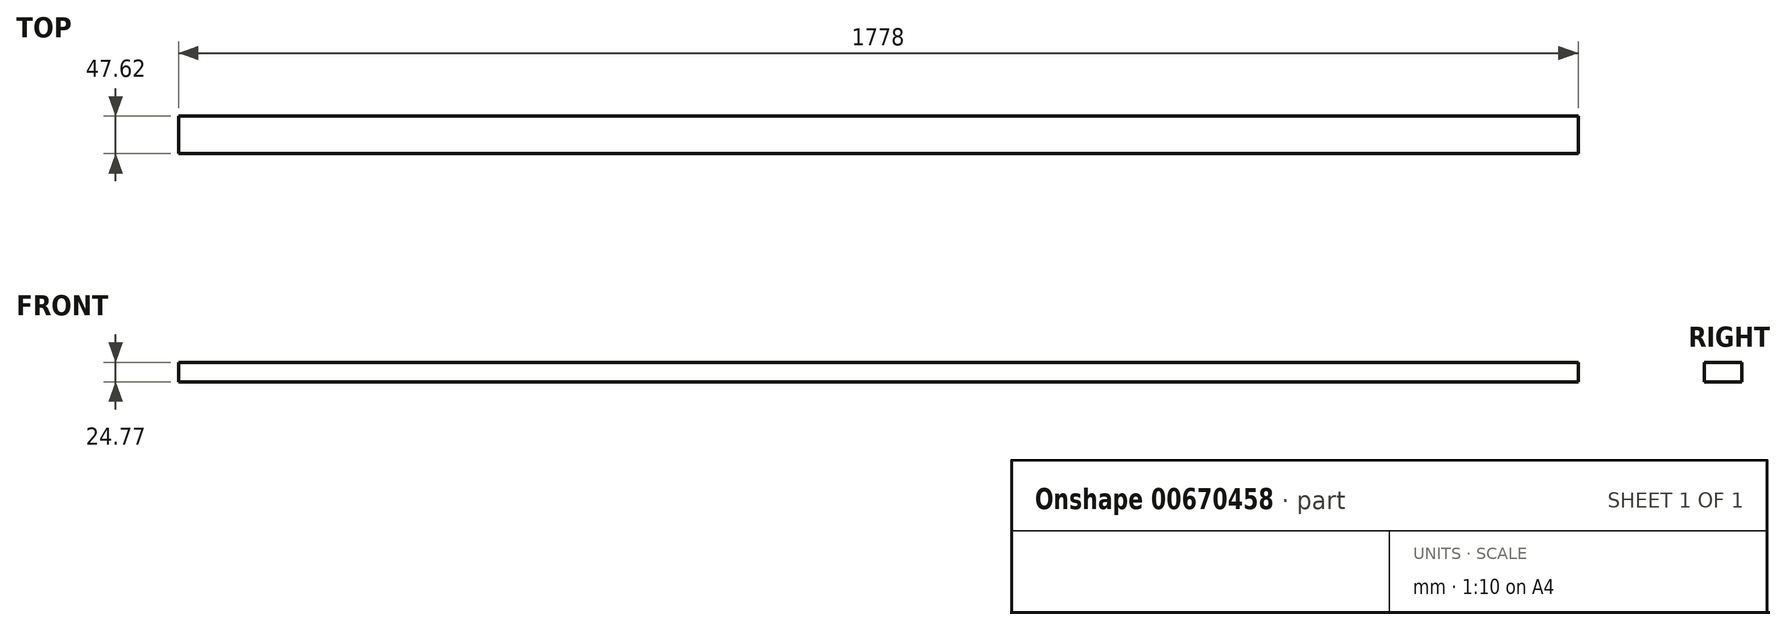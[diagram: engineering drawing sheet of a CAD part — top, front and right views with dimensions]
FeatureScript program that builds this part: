
annotation { "Feature Type Name" : "Feature", "Feature Type Description" : "" }
export const myFeature = defineFeature(function(context is Context, id is Id, definition is map)
    precondition{}
    {
        {
            var Q0;
            Q0=qCreatedBy(makeId("Top.planeOp"),FACE);
            var sketch = newSketch(context, id + "F0", { "sketchPlane" : qUnion([Q0])});
            skLineSegment(sketch, "E0.bottom", {"start": v(0, 0) * mm, "end": v(-1778, 0) * mm});
            skLineSegment(sketch, "E0.top", {"start": v(0, 47.63) * mm, "end": v(-1778, 47.62) * mm});
            skLineSegment(sketch, "E0.left", {"start": v(0, 0) * mm, "end": v(0, 47.63) * mm});
            skLineSegment(sketch, "E0.right", {"start": v(-1778, 0) * mm, "end": v(-1778, 47.62) * mm});
            skSolve(sketch);
        }
        {
            var Q0;
            Q0=makeQuery(id+"F0.imprint","IMPRINT",FACE,{"disambiguationData":[TD([[makeQuery(id+"F0.imprint","IMPRINT",EDGE,{"derivedFrom":sQuery(id+"F0.wireOp",EDGE,"E0.bottom")}),-1.0]])]});
            extrude(context, id + "F1", {"entities" : qUnion([Q0]), "depth" : 24.76 * mm, "offsetDistance" : 25.4 * mm});
        }
    });
